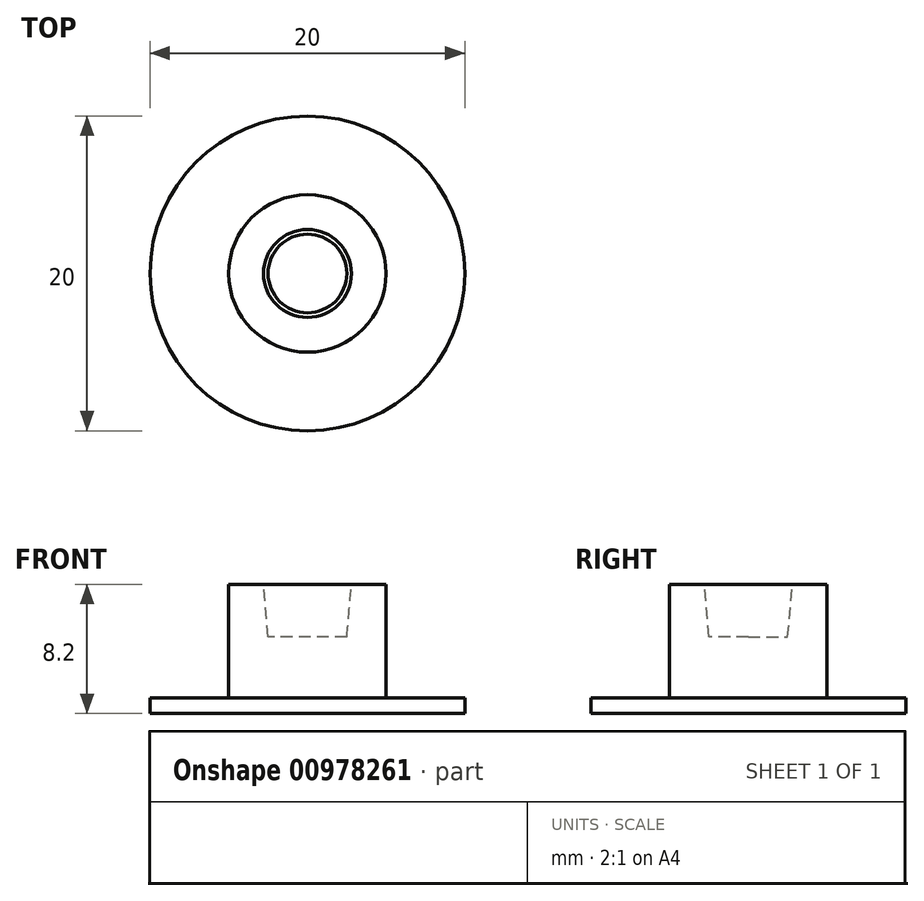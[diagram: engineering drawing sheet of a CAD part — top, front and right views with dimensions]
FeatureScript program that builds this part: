
annotation { "Feature Type Name" : "Feature", "Feature Type Description" : "" }
export const myFeature = defineFeature(function(context is Context, id is Id, definition is map)
    precondition{}
    {
        {
            var Q0;
            Q0=qCreatedBy(makeId("Front.planeOp"),FACE);
            var sketch = newSketch(context, id + "F0", { "sketchPlane" : qUnion([Q0])});
            skLineSegment(sketch, "E0", {"start": v(0, 0) * mm, "end": v(10, 0) * mm});
            skLineSegment(sketch, "E1", {"start": v(10, 0) * mm, "end": v(10, 1) * mm});
            skLineSegment(sketch, "E2", {"start": v(10, 1) * mm, "end": v(5, 1) * mm});
            skLineSegment(sketch, "E3", {"start": v(2.5, 3.85) * mm, "end": v(2.5, 3.85) * mm});
            skLineSegment(sketch, "E4", {"start": v(2.5, 3.85) * mm, "end": v(2.5, 4.85) * mm});
            skLineSegment(sketch, "E5", {"start": v(2.5, 4.85) * mm, "end": v(0, 4.85) * mm});
            skLineSegment(sketch, "E6", {"start": v(0, 4.85) * mm, "end": v(0, 0) * mm});
            skLineSegment(sketch, "E7.bottom", {"start": v(5, 1) * mm, "end": v(5, 1) * mm});
            skLineSegment(sketch, "E7.top", {"start": v(2.5, 1.6) * mm, "end": v(5, 1.6) * mm});
            skLineSegment(sketch, "E7.right", {"start": v(5, 1) * mm, "end": v(5, 1.6) * mm});
            skLineSegment(sketch, "E8", {"start": v(2.5, 1.6) * mm, "end": v(2.5, 3.85) * mm});
            skSolve(sketch);
        }
        {
            var Q0;
            Q0=makeQuery(id+"F0.imprint","IMPRINT",FACE,{"disambiguationData":[TD([[makeQuery(id+"F0.imprint","IMPRINT",EDGE,{"derivedFrom":sQuery(id+"F0.wireOp",EDGE,"E0")}),1.0]])]});
            var Q1;
            Q1=sQuery(id+"F0.wireOp",EDGE,"E6");
            revolve(context, id + "F1", {"surfaceOperationType" : NewSurfaceOperationType.NEW, "entities" : qUnion([Q0]), "axis" : qUnion([Q1]), "revolveType" : RevolveType.FULL});
        }
        {
            var Q0;
            Q0=makeQuery(id+"F1.opRevolve","SWEPT_FACE",FACE,{"disambiguationData":[OSD([sQuery(id+"F0.wireOp",EDGE,"E7.top")])]});
            var sketch = newSketch(context, id + "F2", { "sketchPlane" : qUnion([Q0])});
            skArc(sketch, "E9", {"start": v(3.38, 2.14) * mm, "mid": v(3.84, 1.12) * mm, "end": v(4, 0) * mm});
            skArc(sketch, "E10", {"start": v(2.11, 1.34) * mm, "mid": v(2.4, 0.7) * mm, "end": v(2.5, 0) * mm});
            skLineSegment(sketch, "E11", {"start": v(0, 0) * mm, "end": v(4.22, 2.68) * mm, "construction": true});
            skLineSegment(sketch, "E12", {"start": v(2.11, 1.34) * mm, "end": v(3.38, 2.14) * mm});
            skLineSegment(sketch, "E13", {"start": v(2.5, 0) * mm, "end": v(4, 0) * mm});
            skSolve(sketch);
        }
        {
            var Q0;
            Q0=makeQuery(id+"F2.imprint","IMPRINT",FACE,{"disambiguationData":[TD([[makeQuery(id+"F2.imprint","IMPRINT",EDGE,{"derivedFrom":sQuery(id+"F2.wireOp",EDGE,"E9")}),-1.0]])]});
            extrude(context, id + "F3", {"entities" : qUnion([Q0]), "depth" : 6.6 * mm, "offsetDistance" : 25 * mm});
        }
        {
            var Q0;
            Q0=makeQuery(id+"F3.opExtrude","SWEPT_BODY",BODY,{"disambiguationData":[OSD([sQuery(id+"F2.wireOp",EDGE,"E9"),sQuery(id+"F2.wireOp",EDGE,"E10"),sQuery(id+"F2.wireOp",EDGE,"E12"),sQuery(id+"F2.wireOp",EDGE,"E13")])]});
            var Q1;
            Q1=sQuery(id+"F0.wireOp",EDGE,"E6");
            circularPattern(context, id + "F4", {"operationType" : NewBodyOperationType.ADD, "entities" : qUnion([Q0]), "axis" : qUnion([Q1]), "angle" : 360 * degree, "instanceCount" : 4, "equalSpace" : true});
        }
        {
            var Q0;
            Q0=makeQuery(id+"F1.opRevolve","SWEPT_FACE",FACE,{"disambiguationData":[OSD([sQuery(id+"F0.wireOp",EDGE,"E5")])]});
            var Q1;
            Q1=makeQuery(id+"F3.opExtrude","CAP_FACE",FACE,{"disambiguationData":[OSD([sQuery(id+"F2.wireOp",EDGE,"E9"),sQuery(id+"F2.wireOp",EDGE,"E10"),sQuery(id+"F2.wireOp",EDGE,"E12"),sQuery(id+"F2.wireOp",EDGE,"E13")])],"isStart":false});
            extrude(context, id + "F5", {"entities" : qUnion([Q0]), "operationType" : NewBodyOperationType.REMOVE, "endBound" : BoundingType.UP_TO_SURFACE, "depth" : 3.5 * mm, "endBoundEntityFace" : qUnion([Q1]), "offsetDistance" : 25 * mm, "hasDraft" : true, "draftAngle" : 5 * degree});
        }
    });
